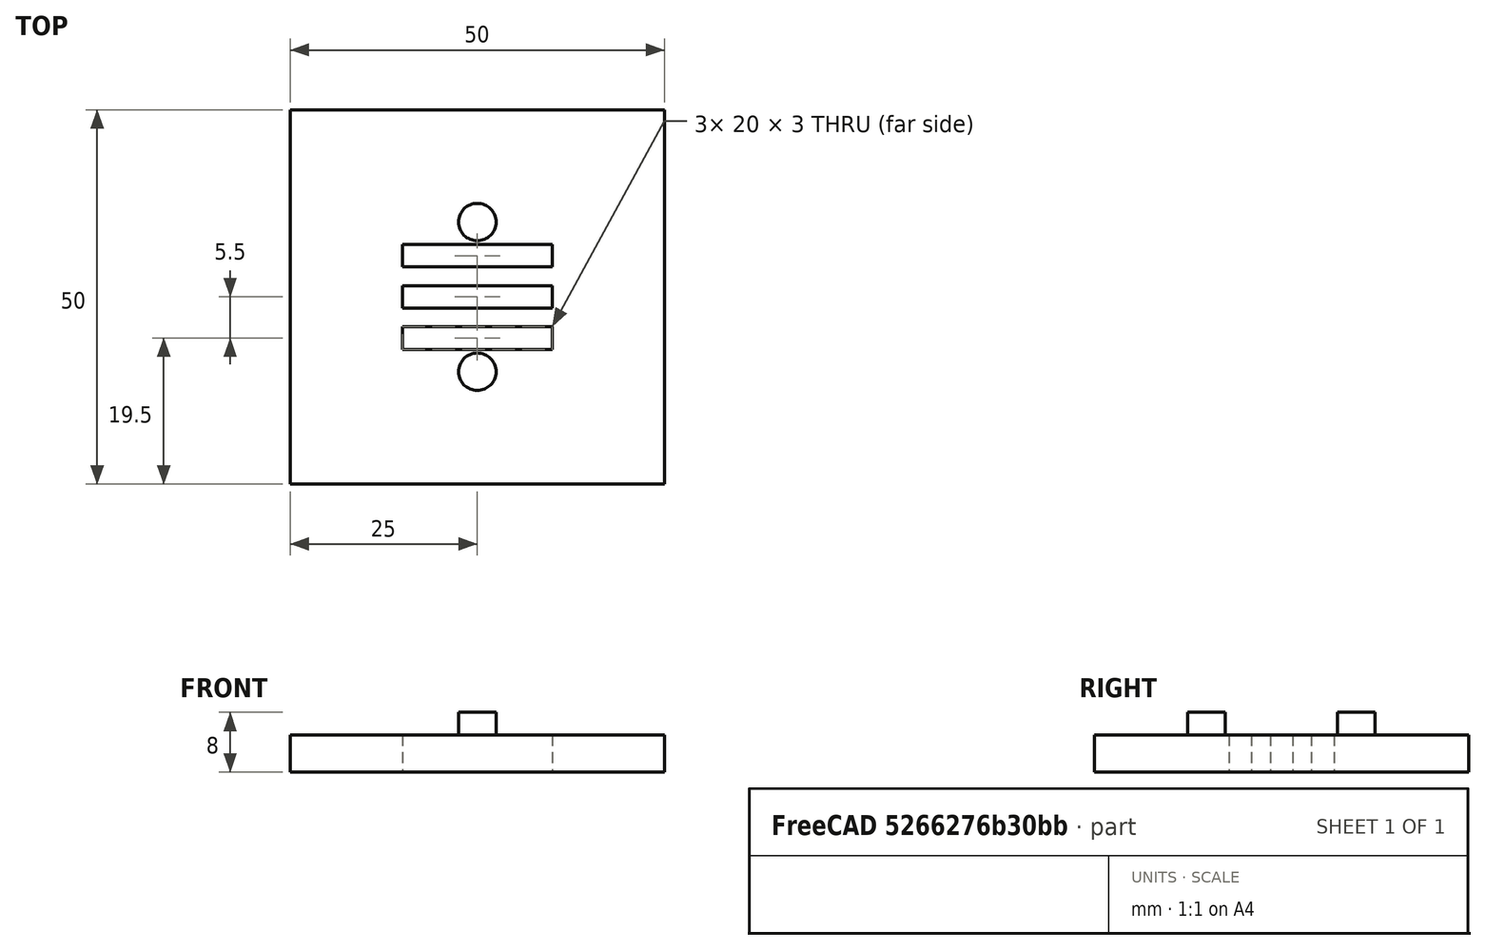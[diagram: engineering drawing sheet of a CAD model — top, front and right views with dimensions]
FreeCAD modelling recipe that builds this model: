
FCSTD DOCUMENT  (FreeCAD 0.16R6712 (Git))
Label: cap1
License: All rights reserved
LicenseURL: http://en.wikipedia.org/wiki/All_rights_reserved
objects: Part::FeaturePython×5, Part::Box×4, Part::Cylinder×2
note: 11 computed .brp shape members not serialized (recipe doc carries the construction recipe); baked Part::Feature solids carry a one-line shape summary decoded from their .brp

FEATURE [Part::Box] Box  label="立方体"
  Height = 5
  Length = 50
  Placement = pos=(-25,-25,0) rot=(0,0,1;0rad)
  Width = 50
FEATURE [Part::Cylinder] Cylinder  label="圆柱体"
  Angle = 360
  Height = 3
  Placement = pos=(0,10,-3) rot=(0,0,1;0rad)
  Radius = 2.5
FEATURE [Part::Cylinder] Cylinder001  label="圆柱体001"
  Angle = 360
  Height = 3
  Placement = pos=(0,-10,-3) rot=(0,0,1;0rad)
  Radius = 2.5
FEATURE [Part::Box] Box017  label="立方体013"
  Height = 5
  Length = 20
  Placement = pos=(-10,4,0) rot=(0,0,1;0rad)
  Width = 3
FEATURE [Part::Box] Box018  label="立方体014"
  Height = 5
  Length = 20
  Placement = pos=(-10,-1.5,0) rot=(0,0,1;0rad)
  Width = 3
FEATURE [Part::Box] Box019  label="立方体015"
  Height = 5
  Length = 20
  Placement = pos=(-10,-7,0) rot=(0,0,1;0rad)
  Width = 3
FEATURE [Part::FeaturePython] Connect  # WARN: FeaturePython — macro-defined, semantics opaque (R4)
  Base = -> Box
  Mode = 1
  Tool = -> Cylinder
FEATURE [Part::FeaturePython] Connect001  # WARN: FeaturePython — macro-defined, semantics opaque (R4)
  Base = -> Connect
  Mode = 1
  Tool = -> Cylinder001
FEATURE [Part::FeaturePython] Cutout  # WARN: FeaturePython — macro-defined, semantics opaque (R4)
  Base = -> Connect001
  Mode = 3
  Tool = -> Box017
FEATURE [Part::FeaturePython] Cutout001  # WARN: FeaturePython — macro-defined, semantics opaque (R4)
  Base = -> Cutout
  Mode = 3
  Tool = -> Box018
FEATURE [Part::FeaturePython] Cutout002  # WARN: FeaturePython — macro-defined, semantics opaque (R4)
  Base = -> Cutout001
  Mode = 3
  Placement = pos=(0,0,0) rot=(0,1,0;3.14159rad)
  Tool = -> Box019
